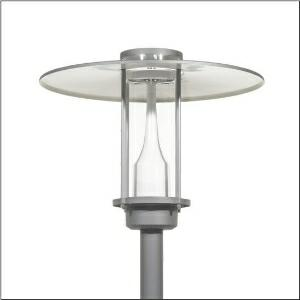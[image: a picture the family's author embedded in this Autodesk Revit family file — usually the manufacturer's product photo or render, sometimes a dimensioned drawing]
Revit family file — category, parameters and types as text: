
# Revit family: city-light_plus_iq___st1_2a_5xa5275af14h_631d
name_source: partatom
category: Lighting Fixtures
units: mm (PartAtom-declared; Revit-internal decimal feet)

## family parameters
Cut with Voids When Loaded = No
Host = Face
Light Source = No
Part Type = Normal
Room Calculation Point = No
Round Connector Dimension = Use Diameter
Shared = No

## types (1)
- --- (1 x LED, 1470 lm, 12.9 W, 2200K)
    Apparent Load = 13 VA
    CIE Flux Codes = 22 62 93 97 100
    Color Rendering = 70
    Color Temperature = 2200K
    Default Elevation = 1800 mm
    Description = City-Light Plus iQ, mast luminaire, Module 540 iQ-SR, primary light control with 3 zone facetted reflector, of plastic, silver coated, highly specular, structured, primary optical cover: cover, of PMMA, transparent, light distribution: ST1.2a, light emission: direct distribution, primary light characteristic: asymmetric, installation type: post-top, LED, High Power LED, rated luminous flux: 1.470lm, luminous efficacy: 114lm/W, light colour: 722, colour temperature: 2200K, control gear: iQ Street-Remote, control: pre-setting: logarithmic dimming characteristic, Street-Remote, Auto-Match, Temp-Guard, Lumen-Switch, Night-Set, Smart-Wire, Light-Fading, Desk-Remote (wireless, voltage-free reading and setting of iQ features in the workshop via application-optimized NFC function/RFID function), optimised constant luminous flux control (CLO 2.0), with terminal, 6-pole, max. 2.5mm², mains connection: 230..240V, AC, 50/60Hz, start of lifetime: 13W, end of service life: 13W, reduction: 6W, luminaire housing, upper part, of glass-fibre reinforced polyester, coated, Siteco® metallic grey (DB 702S), diameter: 750mm, height: 590mm, spigot size: d x l = 76 x 70mm (post-top) | with reducer (optional accessory) 60 x 70mm, mounting height: 3..5m, post-top mast mounting element, of diecast aluminium, coated, Siteco® metallic grey (DB 702S), Module 540 iQ-SR, traffic white (RAL 9016), equipment: standard, protection rating (complete): IP65, insulation class (complete): insulation class II (safety insulation), certification: CE, ENEC, VDE, packaging unit: 1 piece

Light Distribution: ST1.2a
    Height = 590 mm
    Lamp = 1 x LED
    Lamp Light Flux = 1470 lm
    Lamp Power = 12.9 W
    Lamp count = 1
    Length = 750 mm
    Luminous efficacy = 114 lm/W
    Manufacturer = Siteco
    ModVariant = No
    Model = 5XA5275AF14H
    Number of Poles = 1
    OnlyDefault = Yes
    Power Factor = 1
    Product Name = City-Light Plus iQ | ST1.2a
    Product group = mast luminaire | pylon top
    ProductGroupID = 6100
    Protection Class = Protection class II
    Protection Degree = IP 65
    RLX_Detail_Level = 1
    RLX_Emergency_Light_Flux = 0 lm
    RLX_Emergency_Type = 0
    RLX_Emergency_Type_DB = No
    RlxData = <blob elided: 96421 chars, md5=4b49e416>
    Socket = socket
    Standby Power = 0 W
    System Light Flux = 1470 lm
    System Power = 13 W
    Type Comments = factory setting: luminous flux: 100 % | dim-lin: 254 | 516 mA
    Type Image = l_1006456.jpg
    URL = http://relux.com
    VarID = @adj_181613
    Voltage = 0 V
    Weight = 0.00 kg
    Width = 0 mm  [stored 0 ft]

note: [stored X ft] marks values corroborated as IEEE doubles in the binary element streams (Revit-internal decimal feet)

## geometry (parser evidence)
native form markers: Blend x4, Sweep x9
no freeform markers — native parametric forms only
